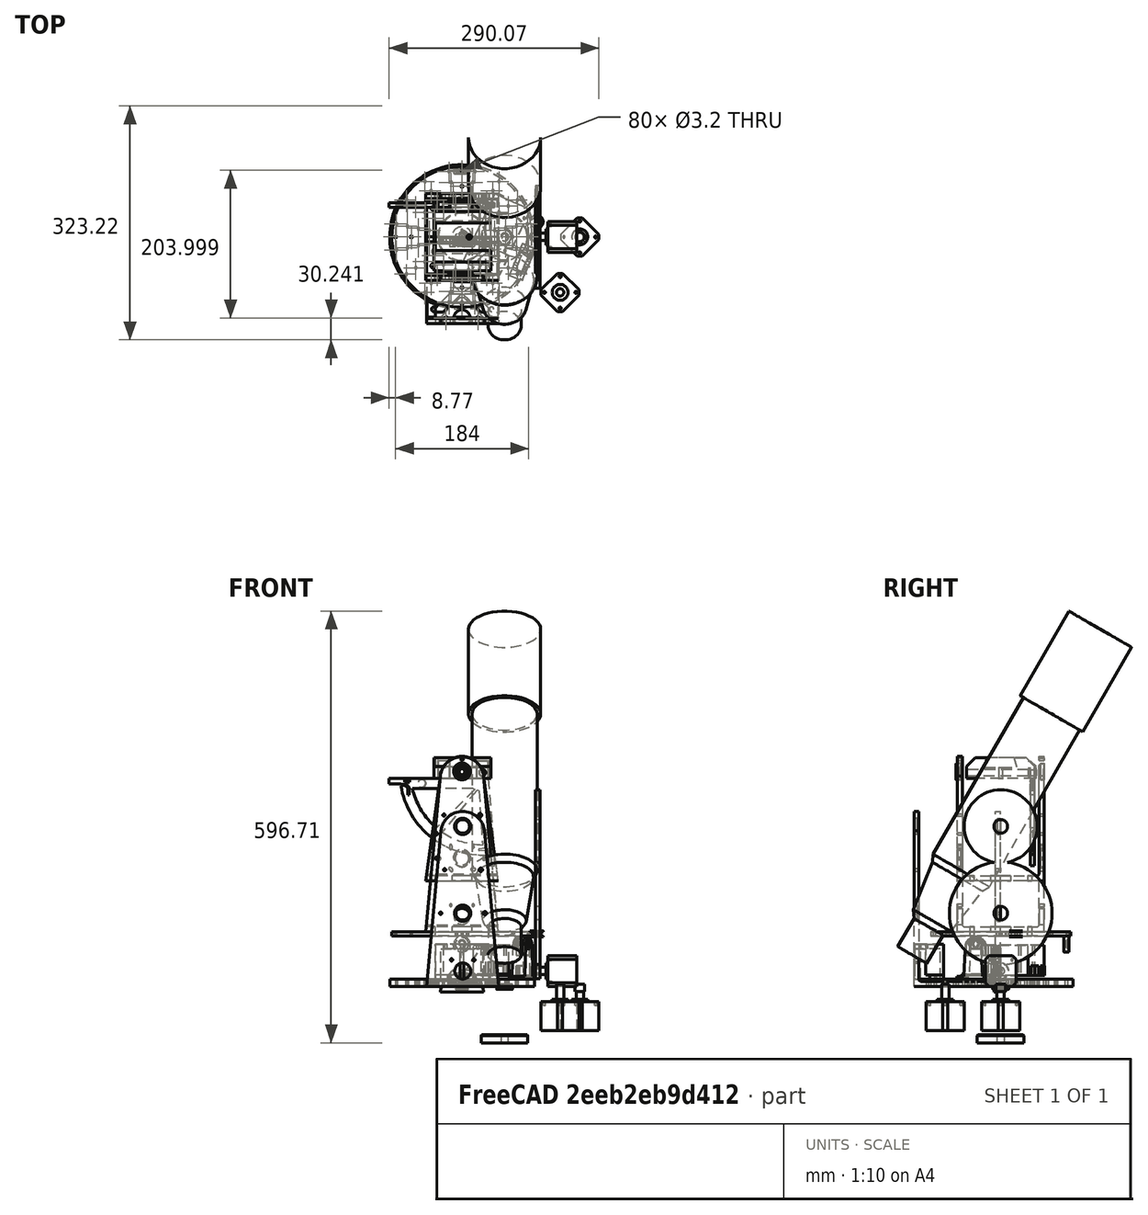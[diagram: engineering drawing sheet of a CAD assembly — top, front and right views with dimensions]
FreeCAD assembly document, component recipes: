
FREECAD ASSEMBLY — COMPONENT RECIPES ("202207 BATS - Begines Astro Tracking System")

This assembly document has 31 components, labeled P0..P30 below (a component is one placed body or linked part). 31 of them carry a construction recipe — the FreeCAD feature program that regenerates the part from scratch, quoted from this document or its linked companion documents; the rest are supplied as boundary geometry only. No exploded tour is included for this assembly.
NOTE — document 2 of 2 of this assembly tour. The two overview renders and the header above are repeated from document 1; the component sections below continue where the previous document stopped.
COMPONENT P21 — recipe-attached ("ALEROS001", modeled in this document).
Construction recipe (the document's own serialized feature program — sketch geometry with constraints, then the solid features built on it; lengths are millimeters unless a unit is written):

FEATURE [Sketcher::SketchObject] Sketch154
  FullyConstrained = true
  Placement = pos=(0,0,120) rot=(0,1,0;1.5708rad)
  sketch-geometry (6):
    g0: LineSegment StartX=7 StartY=252.37 StartZ=0 EndX=113 EndY=252.37 EndZ=0
    g1: LineSegment StartX=113 StartY=252.37 StartZ=0 EndX=113 EndY=79 EndZ=0
    g2: LineSegment StartX=111 StartY=77 StartZ=0 EndX=9 EndY=77 EndZ=0
    g3: LineSegment StartX=7 StartY=79 StartZ=0 EndX=7 EndY=252.37 EndZ=0
    g4: LineSegment StartX=7 StartY=79 StartZ=0 EndX=9 EndY=77 EndZ=0
    g5: LineSegment StartX=113 StartY=79 StartZ=0 EndX=111 EndY=77 EndZ=0
  constraints (18):
    c: Horizontal(g0)
    c: Horizontal(g2)
    c: Vertical(g1)
    c: Vertical(g3)
    c: Coincident(g4,g3)
    c: Coincident(g4,g2)
    c: Coincident(g5,g1)
    c: Coincident(g5,g2)
    c: DistanceY(g-1,g2) = 77
    c: DistanceX(g-1,g3) = 7
    c: DistanceX(g3,g1) = 106
    c: Horizontal(g1,g3)
    c: DistanceX(g3,g2) = 2
    c: DistanceX(g2,g1) = 2
    c: DistanceY(g2,g3) = 2
    c: Coincident(g0,g3)
    c: Coincident(g0,g1)
    c: DistanceY(g0) = 252.37
FEATURE [Sketcher::SketchObject] Sketch155
  FullyConstrained = false
  MapMode = 3
  Placement = pos=(-2.8e-15,0,0) rot=(0,0,1;0rad)
  sketch-geometry (13):
    g0: LineSegment StartX=-50 StartY=70 StartZ=0 EndX=50 EndY=70 EndZ=0
    g1: LineSegment StartX=-50 StartY=70 StartZ=0 EndX=-30 EndY=215 EndZ=0
    g2: LineSegment StartX=50 StartY=70 StartZ=0 EndX=30 EndY=215 EndZ=0
    g3: Circle CenterX=0 CenterY=221.58 CenterZ=0 NormalX=0 NormalY=0 NormalZ=1 AngleXU=0 Radius=9.5
    g4: ArcOfCircle CenterX=0 CenterY=212.08 CenterZ=0 NormalX=0 NormalY=0 NormalZ=1 AngleXU=0 Radius=30.1418 StartAngle=0.0970256 EndAngle=3.04457
    g5: Circle CenterX=0 CenterY=101.58 CenterZ=0 NormalX=0 NormalY=0 NormalZ=1 AngleXU=0 Radius=9.5
    g6: Circle CenterX=-35.6441 CenterY=101.58 CenterZ=0 NormalX=0 NormalY=0 NormalZ=1 AngleXU=0 Radius=1.6
    g7: Circle CenterX=35.6441 CenterY=101.58 CenterZ=0 NormalX=0 NormalY=0 NormalZ=1 AngleXU=0 Radius=1.6
    g8: Circle CenterX=-34.9726 CenterY=135.449 CenterZ=0 NormalX=0 NormalY=0 NormalZ=1 AngleXU=0 Radius=1.6
    g9: Circle CenterX=34.9726 CenterY=135.449 CenterZ=0 NormalX=0 NormalY=0 NormalZ=1 AngleXU=0 Radius=1.6
    g10: GeomPoint X=-45.6441 Y=101.58 Z=0
    g11: GeomPoint X=-40.9726 Y=135.449 Z=0
    g12: Circle CenterX=0 CenterY=238 CenterZ=0 NormalX=0 NormalY=0 NormalZ=1 AngleXU=0 Radius=1.6
  constraints (34):
    c: Coincident(g1,g0)
    c: Coincident(g2,g0)
    c: DistanceX(g0,g0) = 100
    c: DistanceX(g1,g2) = 60
    c: Symmetric(g1,g2,g-2)
    c: PointOnObject(g4,g-2)
    c: Coincident(g4,g1)
    c: PointOnObject(g4,g2)
    c: Radius(g3) = 9.5
    c: DistanceY(g1) = 215
    c: PointOnObject(g4,g3)
    c: Radius(g5) = 9.5
    c: DistanceY(g5,g3) = 120
    c: PointOnObject(g3,g-2)
    c: PointOnObject(g5,g-2)
    c: Equal(g6,g8)
    c: Equal(g6,g9)
    c: Equal(g6,g7)
    c: Radius(g6) = 1.6
    c: Symmetric(g6,g7,g-2)
    c: Symmetric(g8,g9,g-2)
    c: Horizontal(g6,g5)
    c: PointOnObject(g10,g1)
    c: Horizontal(g10,g6)
    c: DistanceX(g10,g6) = 10
    c: PointOnObject(g11,g1)
    c: Horizontal(g8,g11)
    c: DistanceX(g11,g8) = 6
    c: DistanceX(g0) = -50
    c: DistanceY(g0) = 70
    c: Horizontal(g0)
    c: PointOnObject(g12,g-2)
    c: Diameter(g12) = 3.2
    c: DistanceY(g12) = 238
FEATURE [PartDesign::Pad] Pad044  label="bloque"
  Direction = (1,1,1)
  Length = 120
  Length2 = 100
  Placement = pos=(-2.8e-15,0,0) rot=(0,0,1;0rad)
  Profile = -> Sketch155
  Type = 0
FEATURE [PartDesign::Pocket] Pocket098  label="vaciado"
  BaseFeature = -> Pad044
  Length = 304.8
  Length2 = 100
  Midplane = true
  Placement = pos=(-2.8e-15,0,0) rot=(0,0,1;0rad)
  Profile = -> Sketch154
  Type = 0
FEATURE [Sketcher::SketchObject] Sketch152
  ExternalGeometry = -> [Pocket098]
  FullyConstrained = true
  MapMode = 5
  Placement = pos=(-2.8e-15,70,0) rot=(1,0,0;1.5708rad)
  Support = -> [Pocket098]
  sketch-geometry (5):
    g0: Circle CenterX=-40 CenterY=100 CenterZ=0 NormalX=0 NormalY=0 NormalZ=1 AngleXU=0 Radius=3.1
    g1: Circle CenterX=40 CenterY=100 CenterZ=0 NormalX=0 NormalY=0 NormalZ=1 AngleXU=0 Radius=3.1
    g2: Circle CenterX=-40 CenterY=20 CenterZ=0 NormalX=0 NormalY=0 NormalZ=1 AngleXU=0 Radius=3.1
    g3: Circle CenterX=40 CenterY=20 CenterZ=0 NormalX=0 NormalY=0 NormalZ=1 AngleXU=0 Radius=3.1
    g4: Circle CenterX=-1.7e-14 CenterY=60 CenterZ=0 NormalX=0 NormalY=0 NormalZ=1 AngleXU=0 Radius=14
  constraints (12):
    c: Radius(g4) = 14
    c: Symmetric(g-3,g-4,g4)
    c: Equal(g0,g1)
    c: Equal(g0,g2)
    c: Equal(g0,g3)
    c: Radius(g0) = 3.1
    c: Symmetric(g0,g3,g4)
    c: Symmetric(g2,g1,g4)
    c: DistanceX(g0,g1) = 80
    c: DistanceY(g2,g0) = 80
    c: Horizontal(g1,g0)
    c: Vertical(g0,g2)
FEATURE [PartDesign::Pocket] Pocket096  label="huecos base"
  BaseFeature = -> Pocket098
  Length = 8
  Length2 = 100
  Placement = pos=(-2.8e-15,0,0) rot=(0,0,1;0rad)
  Profile = -> Sketch152
  Type = 0
FEATURE [Sketcher::SketchObject] Sketch156
  FullyConstrained = false
  MapMode = 5
  Placement = pos=(-2.8e-15,0,120) rot=(0,0,1;0rad)
  sketch-geometry (16):
    g0: Circle CenterX=-15.5 CenterY=117.08 CenterZ=0 NormalX=0 NormalY=0 NormalZ=1 AngleXU=0 Radius=1.575
    g1: Circle CenterX=15.5 CenterY=117.08 CenterZ=0 NormalX=0 NormalY=0 NormalZ=1 AngleXU=0 Radius=1.575
    g2: Circle CenterX=15.5 CenterY=86.0801 CenterZ=0 NormalX=0 NormalY=0 NormalZ=1 AngleXU=0 Radius=1.575
    g3: Circle CenterX=-15.5 CenterY=86.0801 CenterZ=0 NormalX=0 NormalY=0 NormalZ=1 AngleXU=0 Radius=1.575
    g4: ArcOfCircle CenterX=-15.5 CenterY=118.655 CenterZ=0 NormalX=0 NormalY=0 NormalZ=1 AngleXU=0 Radius=1.75 StartAngle=-2.7e-15 EndAngle=3.14159
    g5: ArcOfCircle CenterX=-15.5 CenterY=115.505 CenterZ=0 NormalX=0 NormalY=0 NormalZ=1 AngleXU=0 Radius=1.75 StartAngle=3.14159 EndAngle=6.28319
    g6: LineSegment StartX=-17.25 StartY=118.655 StartZ=0 EndX=-17.25 EndY=115.505 EndZ=0
    g7: LineSegment StartX=-13.75 StartY=118.655 StartZ=0 EndX=-13.75 EndY=115.505 EndZ=0
    g8: ArcOfCircle CenterX=13.925 CenterY=86.0801 CenterZ=0 NormalX=0 NormalY=0 NormalZ=1 AngleXU=0 Radius=1.75 StartAngle=1.5708 EndAngle=4.71239
    g9: ArcOfCircle CenterX=17.075 CenterY=86.0801 CenterZ=0 NormalX=0 NormalY=0 NormalZ=1 AngleXU=0 Radius=1.75 StartAngle=4.71239 EndAngle=7.85398
    g10: LineSegment StartX=13.925 StartY=84.3301 StartZ=0 EndX=17.075 EndY=84.3301 EndZ=0
    g11: LineSegment StartX=13.925 StartY=87.8301 StartZ=0 EndX=17.075 EndY=87.8301 EndZ=0
    g12: ArcOfCircle CenterX=-16.6137 CenterY=87.1938 CenterZ=0 NormalX=0 NormalY=0 NormalZ=1 AngleXU=0 Radius=1.75 StartAngle=0.785398 EndAngle=3.92699
    g13: ArcOfCircle CenterX=-14.3863 CenterY=84.9664 CenterZ=0 NormalX=0 NormalY=0 NormalZ=1 AngleXU=0 Radius=1.75 StartAngle=3.92699 EndAngle=7.06858
    g14: LineSegment StartX=-17.8511 StartY=85.9563 StartZ=0 EndX=-15.6237 EndY=83.7289 EndZ=0
    g15: LineSegment StartX=-15.3763 StartY=88.4312 StartZ=0 EndX=-13.1489 EndY=86.2038 EndZ=0
  constraints (36):
    c: Diameter(g1) = 3.15
    c: Diameter(g0) = 3.15
    c: Diameter(g3) = 3.15
    c: Diameter(g2) = 3.15
    c: DistanceX(g1) = 15.5
    c: Horizontal(g0,g1)
    c: Vertical(g0,g3)
    c: Vertical(g1,g2)
    c: Horizontal(g2,g3)
    c: Tangent(g4,g7) = 1.5708
    c: Tangent(g4,g6) = -1.5708
    c: Tangent(g6,g5) = -1.5708
    c: Tangent(g7,g5) = 1.5708
    c: Vertical(g6)
    c: Equal(g4,g5)
    c: PointOnObject(g4,g0)
    c: Symmetric(g5,g4,g0)
    c: DistanceX(g5,g5) = 3.5
    c: Tangent(g8,g11) = 1.5708
    c: Tangent(g8,g10) = -1.5708
    c: Tangent(g10,g9) = -1.5708
    c: Tangent(g11,g9) = 1.5708
    c: Horizontal(g10)
    c: Equal(g8,g9)
    c: Symmetric(g8,g9,g2)
    c: PointOnObject(g8,g2)
    c: DistanceY(g9,g9) = 3.5
    c: Tangent(g12,g15) = 1.5708
    c: Tangent(g12,g14) = -1.5708
    c: Tangent(g14,g13) = -1.5708
    c: Tangent(g15,g13) = 1.5708
    c: Equal(g12,g13)
    c: Angle(g14) = -0.785398
    c: Distance(g12,g12) = 3.5
    c: Symmetric(g12,g13,g3)
    c: Distance(g15) = 3.15
FEATURE [PartDesign::Pocket] Pocket099  label="agujeros tornillo nema"
  BaseFeature = -> Pocket096
  Length = 120
  Length2 = 100
  Placement = pos=(-2.8e-15,0,0) rot=(0,0,1;0rad)
  Profile = -> Sketch156
  Type = 0
FEATURE [Sketcher::SketchObject] Sketch157
  ExternalGeometry = -> [Pocket099]
  FullyConstrained = true
  MapMode = 5
  Placement = pos=(-2.8e-15,0,0) rot=(1,0,0;3.14159rad)
  Support = -> [Pocket099]
  sketch-geometry (2):
    g0: Circle CenterX=0 CenterY=-101.58 CenterZ=0 NormalX=0 NormalY=0 NormalZ=1 AngleXU=0 Radius=11.5
    g1: Circle CenterX=0 CenterY=-221.58 CenterZ=0 NormalX=0 NormalY=0 NormalZ=1 AngleXU=0 Radius=11.1
  constraints (4):
    c: Coincident(g0,g-3)
    c: Diameter(g1) = 22.2
    c: Diameter(g0) = 23
    c: Coincident(g1,g-4)
FEATURE [PartDesign::Pocket] Pocket100  label="rebaje derecha"
  BaseFeature = -> Pocket099
  Length = 5
  Length2 = -100
  Placement = pos=(-2.8e-15,0,0) rot=(0,0,1;0rad)
  Profile = -> Sketch157
  Type = 0
FEATURE [Sketcher::SketchObject] Sketch158
  ExternalGeometry = -> [Pocket100]
  FullyConstrained = true
  MapMode = 5
  Placement = pos=(-2.8e-15,0,120) rot=(0,0,1;0rad)
  Support = -> [Pocket100]
  sketch-geometry (2):
    g0: Circle CenterX=0 CenterY=221.58 CenterZ=0 NormalX=0 NormalY=0 NormalZ=1 AngleXU=0 Radius=11.1
    g1: Circle CenterX=0 CenterY=101.58 CenterZ=0 NormalX=0 NormalY=0 NormalZ=1 AngleXU=0 Radius=11.5
  constraints (4):
    c: Diameter(g0) = 22.2
    c: Diameter(g1) = 23
    c: Coincident(g0,g-3)
    c: Coincident(g1,g-4)
FEATURE [PartDesign::Pocket] Pocket101  label="rebaje izquierda"
  BaseFeature = -> Pocket100
  Length = 5
  Length2 = 100
  Placement = pos=(-2.8e-15,0,0) rot=(0,0,1;0rad)
  Profile = -> Sketch158
  Type = 0
FEATURE [PartDesign::Chamfer] Chamfer026
  Angle = 45
  Base = -> Pocket101 [Edge61,Edge48,Edge39,Edge26]
  BaseFeature = -> Pocket101
  ChamferType = 0
  FlipDirection = false
  Placement = pos=(-2.8e-15,0,0) rot=(0,0,1;0rad)
  Size = 0.5
  Size2 = 1
  SupportTransform = false
FEATURE [PartDesign::Body] Body034  label="ALEROS001"
  Group = -> [Sketch155,Pad044,Sketch154,Pocket098,Sketch152,Pocket096,Sketch156,Pocket099,Sketch157,Pocket100,Sketch158,Pocket101,Chamfer026]
  Origin = -> Origin034
  Placement = pos=(0,60,75.6) rot=(1,0,0;1.5708rad)
  Tip = -> Chamfer026
COMPONENT P22 — recipe-attached ("SOPORTE002", modeled in this document).
Construction recipe (the document's own serialized feature program — sketch geometry with constraints, then the solid features built on it; lengths are millimeters unless a unit is written):

FEATURE [Sketcher::SketchObject] Sketch088
  FullyConstrained = true
  MapMode = 5
  Placement = pos=(0,0,0) rot=(0.57735,0.57735,0.57735;2.0944rad)
  Support = -> [YZ_Plane020]
  sketch-geometry (16):
    g0: ArcOfCircle CenterX=0 CenterY=0 CenterZ=0 NormalX=0 NormalY=0 NormalZ=1 AngleXU=0 Radius=12 StartAngle=0.25268 EndAngle=2.88891
    g1: LineSegment StartX=-11.619 StartY=3 StartZ=0 EndX=-14 EndY=-41 EndZ=0
    g2: LineSegment StartX=14 StartY=-41 StartZ=0 EndX=11.619 EndY=3 EndZ=0
    g3: LineSegment StartX=14 StartY=-41 StartZ=0 EndX=24 EndY=-41 EndZ=0
    g4: LineSegment StartX=24 StartY=-41 StartZ=0 EndX=24 EndY=-45 EndZ=0
    g5: LineSegment StartX=24 StartY=-45 StartZ=0 EndX=-24 EndY=-45 EndZ=0
    g6: LineSegment StartX=-24 StartY=-45 StartZ=0 EndX=-24 EndY=-41 EndZ=0
    g7: LineSegment StartX=-24 StartY=-41 StartZ=0 EndX=-14 EndY=-41 EndZ=0
    g8: LineSegment StartX=7.62102 StartY=3.5 StartZ=0 EndX=3.81051 EndY=10.1 EndZ=0
    g9: LineSegment StartX=3.81051 StartY=10.1 StartZ=0 EndX=-3.81051 EndY=10.1 EndZ=0
    g10: LineSegment StartX=-3.81051 StartY=10.1 StartZ=0 EndX=-7.62102 EndY=3.5 EndZ=0
    g11: LineSegment StartX=-7.62102 StartY=3.5 StartZ=0 EndX=-3.81051 EndY=-3.1 EndZ=0
    g12: LineSegment StartX=-3.81051 StartY=-3.1 StartZ=0 EndX=3.81051 EndY=-3.1 EndZ=0
    g13: LineSegment StartX=3.81051 StartY=-3.1 StartZ=0 EndX=7.62102 EndY=3.5 EndZ=0
    g14: Circle CenterX=0 CenterY=3.5 CenterZ=0 NormalX=0 NormalY=0 NormalZ=1 AngleXU=0 Radius=7.62102
    g15: GeomPoint X=0 Y=12 Z=0
  constraints (43):
    c: Coincident(g2,g0)
    c: Coincident(g0,g1)
    c: Symmetric(g2,g1,g-2)
    c: Coincident(g2,g3)
    c: Coincident(g3,g4)
    c: Coincident(g4,g5)
    c: Coincident(g5,g6)
    c: Coincident(g6,g7)
    c: Coincident(g7,g1)
    c: Horizontal(g7)
    c: Vertical(g6)
    c: Vertical(g4)
    c: DistanceY(g0,g0) = 3
    c: Radius(g0) = 12
    c: Horizontal(g0,g0)
    c: Symmetric(g3,g6,g-2)
    c: DistanceY(g4,g4) = 4
    c: DistanceY(g4,g0) = 45
    c: DistanceX(g1,g2) = 28
    c: DistanceX(g6,g3) = 48
    c: Coincident(g8,g9)
    c: Coincident(g9,g10)
    c: Coincident(g10,g11)
    c: Coincident(g11,g12)
    c: Coincident(g12,g13)
    c: Coincident(g13,g8)
    c: Equal(g8, g9-g13) x5
    c: PointOnObject(g8,g14)
    c: PointOnObject(g9,g14)
    c: PointOnObject(g10,g14)
    c: PointOnObject(g11,g14)
    c: PointOnObject(g12,g14)
    c: PointOnObject(g13,g14)
    c: Horizontal(g5)
    c: Distance(g10,g12) = 13.2
    c: Coincident(g-1,g0)
    c: PointOnObject(g14,g-2)
    c: DistanceY(g0,g14) = 3.5
    c: Horizontal(g9)
    c: Radius(g14) = 7.62102
    c: PointOnObject(g15,g0)
    c: PointOnObject(g15,g-2)
    c: DistanceY(g14,g15) = 8.5
FEATURE [PartDesign::Pad] Pad030
  Direction = (1,1,1)
  Length = 19
  Length2 = 100
  Placement = pos=(0,0,0) rot=(0.57735,0.57735,0.57735;2.0944rad)
  Profile = -> Sketch088
  Type = 0
FEATURE [Sketcher::SketchObject] Sketch090
  ExternalGeometry = -> [Pad030]
  FullyConstrained = true
  MapMode = 5
  Placement = pos=(0,0,0) rot=(1,0,0;1.5708rad)
  Support = -> [XZ_Plane020]
  sketch-geometry (4):
    g0: LineSegment StartX=5 StartY=15 StartZ=0 EndX=14 EndY=15 EndZ=0
    g1: LineSegment StartX=14 StartY=15 StartZ=0 EndX=14 EndY=-12 EndZ=0
    g2: LineSegment StartX=14 StartY=-12 StartZ=0 EndX=5 EndY=-12 EndZ=0
    g3: LineSegment StartX=5 StartY=-12 StartZ=0 EndX=5 EndY=15 EndZ=0
  constraints (13):
    c: Coincident(g0,g1)
    c: Coincident(g1,g2)
    c: Coincident(g2,g3)
    c: Coincident(g3,g0)
    c: Horizontal(g0)
    c: Horizontal(g2)
    c: Vertical(g1)
    c: Vertical(g3)
    c: DistanceX(g0,g0) = 9
    c: DistanceX(g-4,g0) = 5
    c: DistanceX(g0,g-5) = 5
    c: DistanceY(g-4,g0) = 12
    c: DistanceY(g1,g-5) = 15
FEATURE [PartDesign::Pocket] Pocket054
  BaseFeature = -> Pad030
  Length = 30
  Length2 = 100
  Midplane = true
  Placement = pos=(0,0,0) rot=(0.57735,0.57735,0.57735;2.0944rad)
  Profile = -> Sketch090
  Type = 0
FEATURE [Sketcher::SketchObject] Sketch089
  ExternalGeometry = -> [Pocket054]
  FullyConstrained = true
  MapMode = 5
  Placement = pos=(1.26e-14,-1.98e-14,-45) rot=(0.707107,0.707107,0;3.14159rad)
  Support = -> [Pocket054]
  sketch-geometry (2):
    g0: Circle CenterX=-18 CenterY=9.5 CenterZ=0 NormalX=0 NormalY=0 NormalZ=1 AngleXU=0 Radius=1.6
    g1: Circle CenterX=18 CenterY=9.5 CenterZ=0 NormalX=0 NormalY=0 NormalZ=1 AngleXU=0 Radius=1.6
  constraints (6):
    c: Equal(g0,g1)
    c: Radius(g0) = 1.6
    c: Symmetric(g0,g1,g-2)
    c: DistanceX(g0,g1) = 36
    c: DistanceY(g-4,g-4) = 19
    c: DistanceY(g-4,g0) = 9.5
FEATURE [PartDesign::Pocket] Pocket053
  BaseFeature = -> Pocket054
  Length = 5
  Length2 = 100
  Placement = pos=(0,0,0) rot=(0.57735,0.57735,0.57735;2.0944rad)
  Profile = -> Sketch089
  Type = 0
FEATURE [PartDesign::Chamfer] Chamfer010
  Angle = 45
  Base = -> Pocket053 [Edge49,Edge39,Edge37,Edge46]
  BaseFeature = -> Pocket053
  ChamferType = 0
  FlipDirection = false
  Placement = pos=(0,0,0) rot=(0.57735,0.57735,0.57735;2.0944rad)
  Size = 0.3
  Size2 = 1
  SupportTransform = false
FEATURE [PartDesign::Body] Body020  label="SOPORTE001"
  Group = -> [Sketch088,Pad030,Sketch090,Pocket054,Sketch089,Pocket053,Chamfer010]
  Origin = -> Origin020
  Placement = pos=(74.8149,-31.0129,55.1) rot=(0,0,-1;0.392699rad)
  Tip = -> Chamfer010
COMPONENT P23 — same part as P22; its construction recipe is shown at P22.
COMPONENT P24 — recipe-attached ("BEARING 22x8x7w001", modeled in this document).
Construction recipe (the document's own serialized feature program — sketch geometry with constraints, then the solid features built on it; lengths are millimeters unless a unit is written):

FEATURE [Sketcher::SketchObject] Sketch033
  FullyConstrained = true
  MapMode = 5
  Support = -> [XY_Plane008]
  sketch-geometry (2):
    g0: Circle CenterX=0 CenterY=0 CenterZ=0 NormalX=0 NormalY=0 NormalZ=1 AngleXU=0 Radius=4
    g1: Circle CenterX=0 CenterY=0 CenterZ=0 NormalX=0 NormalY=0 NormalZ=1 AngleXU=0 Radius=11
  constraints (4):
    c: Coincident(g0,g-1)
    c: Coincident(g1,g0)
    c: Radius(g0) = 4
    c: Radius(g1) = 11
FEATURE [PartDesign::Pad] Pad012
  Direction = (1,1,1)
  Length = 7
  Length2 = 100
  Profile = -> Sketch033
  Type = 0
FEATURE [Sketcher::SketchObject] Sketch035
  FullyConstrained = true
  MapMode = 5
  Placement = pos=(0,0,7) rot=(0,0,1;0rad)
  Support = -> [Pad012]
  sketch-geometry (2):
    g0: Circle CenterX=0 CenterY=0 CenterZ=0 NormalX=0 NormalY=0 NormalZ=1 AngleXU=0 Radius=5.5
    g1: Circle CenterX=0 CenterY=0 CenterZ=0 NormalX=0 NormalY=0 NormalZ=1 AngleXU=0 Radius=5.6
  constraints (4):
    c: Coincident(g0,g-1)
    c: Coincident(g1,g0)
    c: Radius(g0) = 5.5
    c: Radius(g1) = 5.6
FEATURE [PartDesign::Pocket] Pocket016
  BaseFeature = -> Pad012
  Length = 3
  Length2 = 100
  Midplane = true
  Profile = -> Sketch035
  Reversed = true
  Type = 0
FEATURE [Sketcher::SketchObject] Sketch034
  FullyConstrained = true
  MapMode = 5
  Placement = pos=(0,0,0) rot=(1,0,0;3.14159rad)
  Support = -> [Pocket016]
  sketch-geometry (2):
    g0: Circle CenterX=0 CenterY=0 CenterZ=0 NormalX=0 NormalY=0 NormalZ=1 AngleXU=0 Radius=5.5
    g1: Circle CenterX=0 CenterY=0 CenterZ=0 NormalX=0 NormalY=0 NormalZ=1 AngleXU=0 Radius=5.6
  constraints (4):
    c: Coincident(g0,g-1)
    c: Coincident(g1,g0)
    c: Radius(g0) = 5.5
    c: Radius(g1) = 5.6
FEATURE [PartDesign::Pocket] Pocket019
  BaseFeature = -> Pocket016
  Length = 3
  Length2 = 100
  Profile = -> Sketch034
  Type = 0
FEATURE [Sketcher::SketchObject] Sketch032
  FullyConstrained = true
  MapMode = 5
  Placement = pos=(0,0,7) rot=(0,0,1;0rad)
  Support = -> [Pocket019]
  sketch-geometry (2):
    g0: Circle CenterX=0 CenterY=0 CenterZ=0 NormalX=0 NormalY=0 NormalZ=1 AngleXU=0 Radius=9
    g1: Circle CenterX=0 CenterY=0 CenterZ=0 NormalX=0 NormalY=0 NormalZ=1 AngleXU=0 Radius=9.1
  constraints (4):
    c: Coincident(g0,g-1)
    c: Coincident(g1,g0)
    c: Radius(g0) = 9
    c: Radius(g1) = 9.1
FEATURE [PartDesign::Pocket] Pocket018
  BaseFeature = -> Pocket019
  Length = 1
  Length2 = 100
  Profile = -> Sketch032
  Type = 0
FEATURE [Sketcher::SketchObject] Sketch031
  FullyConstrained = true
  MapMode = 5
  Placement = pos=(0,0,0) rot=(1,0,0;3.14159rad)
  Support = -> [Pocket018]
  sketch-geometry (2):
    g0: Circle CenterX=0 CenterY=0 CenterZ=0 NormalX=0 NormalY=0 NormalZ=1 AngleXU=0 Radius=9
    g1: Circle CenterX=0 CenterY=0 CenterZ=0 NormalX=0 NormalY=0 NormalZ=1 AngleXU=0 Radius=9.1
  constraints (4):
    c: Coincident(g0,g-1)
    c: Coincident(g1,g0)
    c: Radius(g0) = 9
    c: Radius(g1) = 9.1
FEATURE [PartDesign::Pocket] Pocket017
  BaseFeature = -> Pocket018
  Length = 1
  Length2 = 100
  Profile = -> Sketch031
  Type = 0
FEATURE [PartDesign::Fillet] Fillet002
  Base = -> Pocket017 [Edge2,Edge3]
  BaseFeature = -> Pocket017
  Radius = 0.2
  SupportTransform = false
FEATURE [PartDesign::Body] Body008  label="BEARING 22x8x7w000"
  Group = -> [Sketch033,Pad012,Sketch035,Pocket016,Sketch034,Pocket019,Sketch032,Pocket018,Sketch031,Pocket017,Fillet002]
  Origin = -> Origin008
  Placement = pos=(-7.6e-14,94.2,58.6) rot=(0.57735,-0.57735,0.57735;2.0944rad)
  Tip = -> Fillet002
COMPONENT P25 — same part as P24; its construction recipe is shown at P24.
COMPONENT P26 — recipe-attached ("POLEA002", modeled in this document).
Construction recipe (the document's own serialized feature program — sketch geometry with constraints, then the solid features built on it; lengths are millimeters unless a unit is written):

FEATURE [Sketcher::SketchObject] Sketch092
  FullyConstrained = true
  MapMode = 5
  Placement = pos=(0,0,0) rot=(0.57735,0.57735,0.57735;2.0944rad)
  Support = -> [YZ_Plane022]
  sketch-geometry (8):
    g0: LineSegment StartX=1.55 StartY=4.1 StartZ=0 EndX=1.55 EndY=-4.1 EndZ=0
    g1: LineSegment StartX=1.55 StartY=-4.1 StartZ=0 EndX=9 EndY=-4.1 EndZ=0
    g2: LineSegment StartX=9 StartY=-4.1 StartZ=0 EndX=9 EndY=-3.1 EndZ=0
    g3: LineSegment StartX=9 StartY=-3.1 StartZ=0 EndX=6 EndY=-3.1 EndZ=0
    g4: LineSegment StartX=6 StartY=-3.1 StartZ=0 EndX=6 EndY=3.1 EndZ=0
    g5: LineSegment StartX=6 StartY=3.1 StartZ=0 EndX=9 EndY=3.1 EndZ=0
    g6: LineSegment StartX=9 StartY=3.1 StartZ=0 EndX=9 EndY=4.1 EndZ=0
    g7: LineSegment StartX=9 StartY=4.1 StartZ=0 EndX=1.55 EndY=4.1 EndZ=0
  constraints (22):
    c: Coincident(g0,g1)
    c: Horizontal(g1)
    c: Coincident(g1,g2)
    c: Vertical(g2)
    c: Coincident(g2,g3)
    c: Horizontal(g3)
    c: Coincident(g3,g4)
    c: Coincident(g4,g5)
    c: Horizontal(g5)
    c: Coincident(g5,g6)
    c: Vertical(g6)
    c: Coincident(g6,g7)
    c: Coincident(g7,g0)
    c: Horizontal(g7)
    c: Vertical(g5,g2)
    c: DistanceX(g-1,g0) = 1.55
    c: DistanceX(g-1,g4) = 6
    c: DistanceY(g0,g0) = 8.2
    c: Symmetric(g0,g0,g-1)
    c: DistanceY(g3,g4) = 6.2
    c: Symmetric(g4,g3,g-1)
    c: DistanceX(g-1,g6) = 9
FEATURE [PartDesign::Revolution] Revolution002
  Angle = 360
  Axis = (-2e-16,3e-16,1)
  Base = (0,0,0)
  Placement = pos=(0,0,0) rot=(0.57735,0.57735,0.57735;2.0944rad)
  Profile = -> Sketch092
  ReferenceAxis = -> Sketch092 [V_Axis]
  Reversed = true
FEATURE [PartDesign::Body] Body022  label="POLEA001"
  Group = -> [Sketch092,Revolution002]
  Origin = -> Origin022
  Placement = pos=(103.2,21.05,72.6) rot=(0,0,1;0rad)
  Tip = -> Revolution002
COMPONENT P27 — same part as P26; its construction recipe is shown at P26.
COMPONENT P28 — same part as P26; its construction recipe is shown at P26.
COMPONENT P29 — same part as P26; its construction recipe is shown at P26.
COMPONENT P30 — same part as P26; its construction recipe is shown at P26.
PROVENANCE & LICENSES
A FreeCAD (.FCStd) document from a public repository crawl; recipes are the document's own serialized feature recipes (and, for linked parts, companion documents' recipes).
License: as declared in the source repository (recorded in the dataset sidecar).
